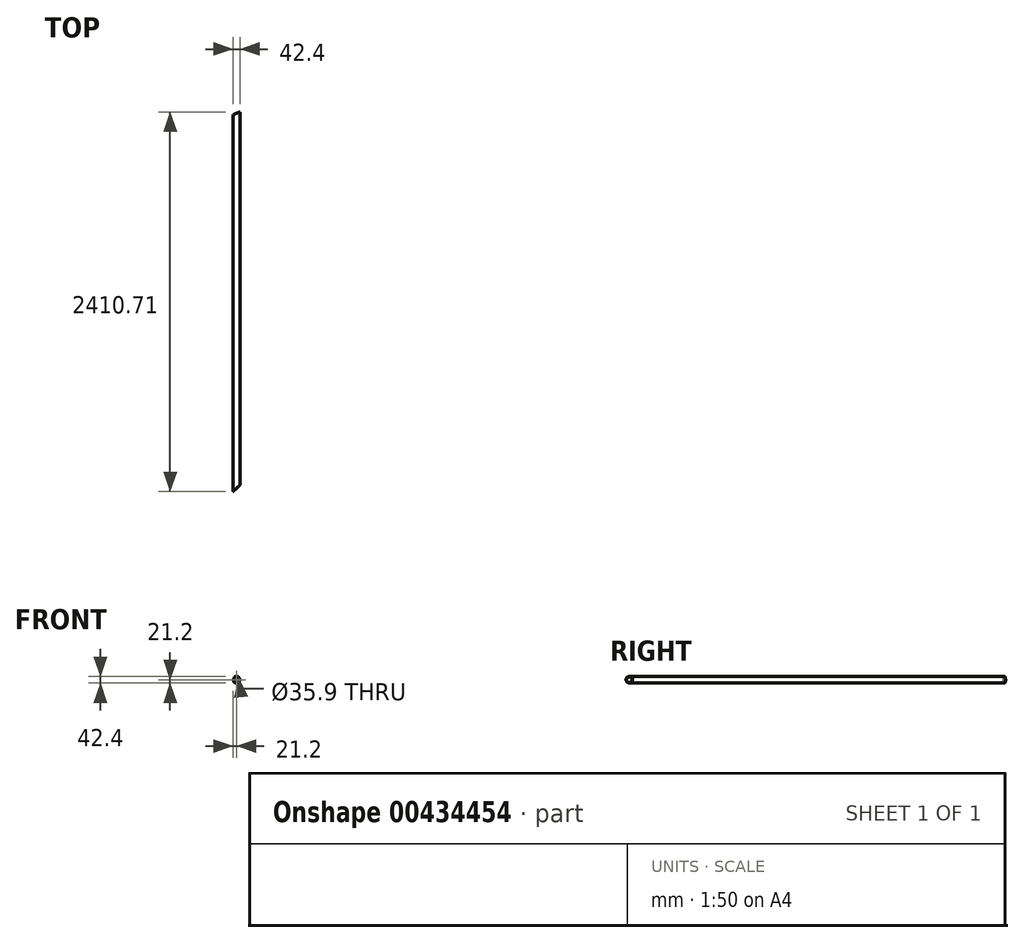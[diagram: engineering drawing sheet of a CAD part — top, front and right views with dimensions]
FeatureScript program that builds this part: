
annotation { "Feature Type Name" : "Feature", "Feature Type Description" : "" }
export const myFeature = defineFeature(function(context is Context, id is Id, definition is map)
    precondition{}
    {
        {
            var Q0;
            Q0=qCreatedBy(makeId("Front.planeOp"),FACE);
            var sketch = newSketch(context, id + "F0", { "sketchPlane" : qUnion([Q0])});
            skCircle(sketch, "E0", {"center": v(0, 0) * mm, "radius": 21.2 * mm});
            skCircle(sketch, "E1", {"center": v(0, 0) * mm, "radius": 17.95 * mm});
            skSolve(sketch);
        }
        {
            var Q0;
            Q0=qSketchRegion(id+"F0",true);
            extrude(context, id + "F1", {"entities" : qUnion([Q0]), "depth" : 2500 * mm, "offsetDistance" : 25 * mm});
        }
        {
            var Q0;
            Q0=qCreatedBy(makeId("Top.planeOp"),FACE);
            var sketch = newSketch(context, id + "F2", { "sketchPlane" : qUnion([Q0])});
            skLineSegment(sketch, "E2", {"start": v(-21.2, -16.88) * mm, "end": v(21.2, 0) * mm});
            skLineSegment(sketch, "E3", {"start": v(21.2, 0) * mm, "end": v(-21.2, 0) * mm});
            skLineSegment(sketch, "E4", {"start": v(-21.2, 0) * mm, "end": v(-21.2, -16.88) * mm});
            skSolve(sketch);
        }
        {
            var Q0;
            Q0=qSketchRegion(id+"F2",true);
            extrude(context, id + "F3", {"entities" : qUnion([Q0]), "operationType" : NewBodyOperationType.REMOVE, "endBound" : BoundingType.THROUGH_ALL, "oppositeDirection" : true, "depth" : 25 * mm, "offsetDistance" : 25 * mm, "hasSecondDirection" : true, "secondDirectionBound" : SecondDirectionBoundingType.THROUGH_ALL, "secondDirectionOppositeDirection" : false, "secondDirectionDepth" : 25 * mm});
        }
        {
            var Q0;
            Q0=qCreatedBy(makeId("Top.planeOp"),FACE);
            var sketch = newSketch(context, id + "F4", { "sketchPlane" : qUnion([Q0])});
            skLineSegment(sketch, "E5", {"start": v(21.2, 0) * mm, "end": v(1204.68, -1250.86) * mm, "construction": true});
            skLineSegment(sketch, "E6", {"start": v(1204.68, -1250.86) * mm, "end": v(21.2, -2370.6) * mm, "construction": true});
            skLineSegment(sketch, "E7", {"start": v(21.2, -2370.6) * mm, "end": v(21.2, 0) * mm, "construction": true});
            skLineSegment(sketch, "E8", {"start": v(21.2, -2370.6) * mm, "end": v(-21.2, -2410.71) * mm});
            skLineSegment(sketch, "E9", {"start": v(-21.2, -2410.71) * mm, "end": v(-21.2, -2500) * mm});
            skLineSegment(sketch, "E10", {"start": v(-21.2, -2500) * mm, "end": v(21.2, -2500) * mm});
            skLineSegment(sketch, "E11", {"start": v(21.2, -2500) * mm, "end": v(21.2, -2370.6) * mm});
            skSolve(sketch);
        }
        {
            var Q0;
            Q0 = qSketchRegion(id + "F4", true);
            extrude(context, id + "F5", {"entities" : qUnion([Q0]), "operationType" : NewBodyOperationType.REMOVE, "endBound" : BoundingType.THROUGH_ALL, "oppositeDirection" : true, "depth" : 25 * mm, "offsetDistance" : 25 * mm, "hasSecondDirection" : true, "secondDirectionBound" : SecondDirectionBoundingType.THROUGH_ALL, "secondDirectionOppositeDirection" : false, "secondDirectionDepth" : 25 * mm});
        }
    });
